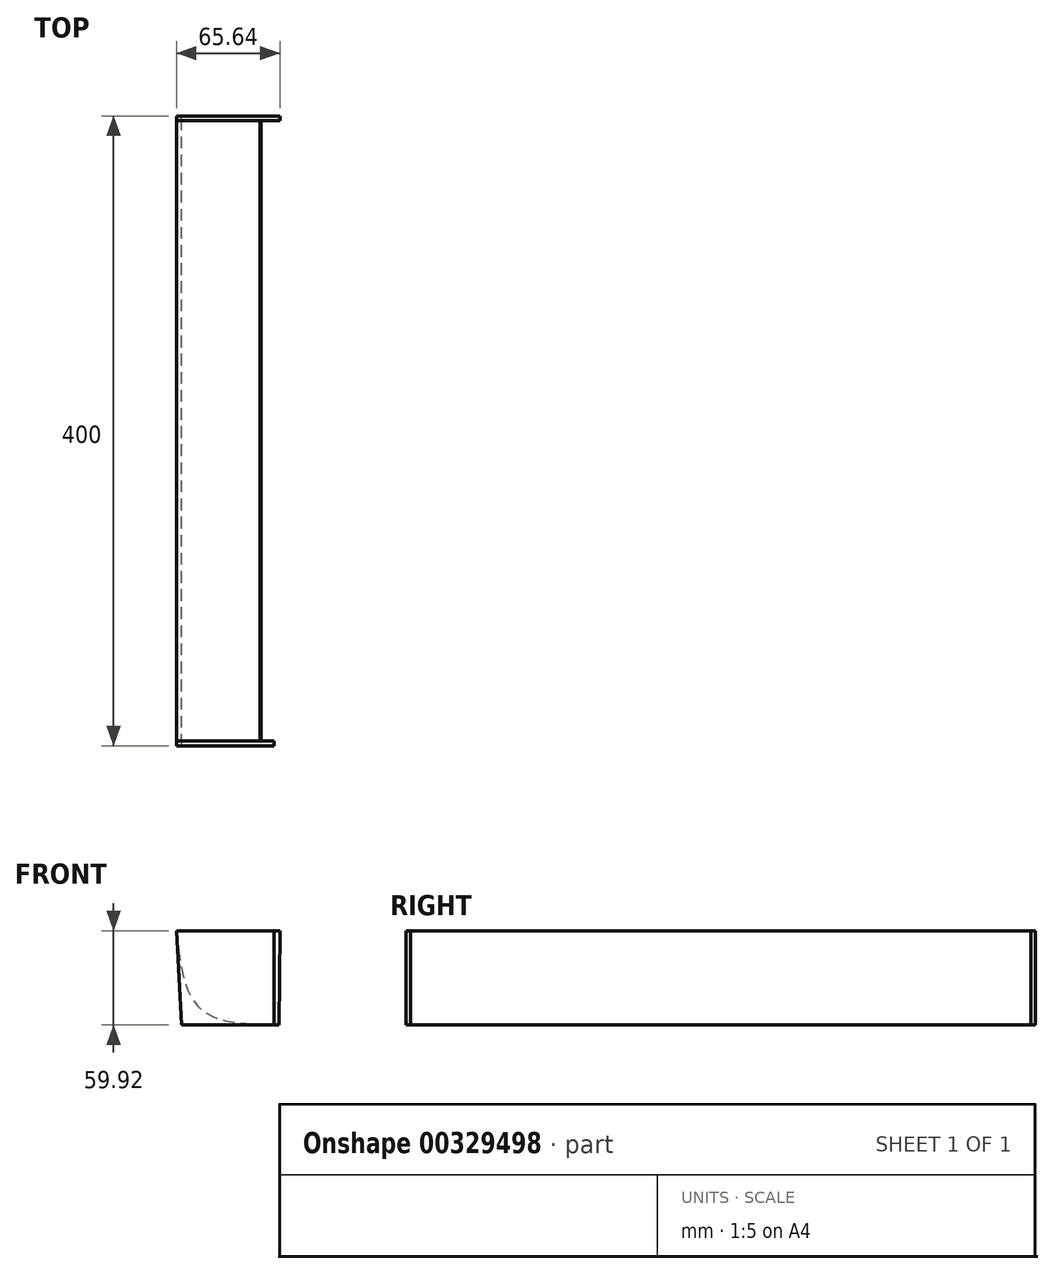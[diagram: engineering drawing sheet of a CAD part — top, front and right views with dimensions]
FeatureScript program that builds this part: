
annotation { "Feature Type Name" : "Feature", "Feature Type Description" : "" }
export const myFeature = defineFeature(function(context is Context, id is Id, definition is map)
    precondition{}
    {
        {
            var Q0;
            Q0=qCreatedBy(makeId("Front.planeOp"),FACE);
            var sketch = newSketch(context, id + "F0", { "sketchPlane" : qUnion([Q0])});
            skLineSegment(sketch, "E0", {"start": v(3.08, 0) * mm, "end": v(53.01, 0) * mm});
            skFitSpline(sketch, "E1", {"points": [v(0, 59.92) * mm, v(25.95, 4.2) * mm, v(53.01, 0) * mm], "startDerivative": vector(13.48, -155.54) * mm, "endDerivative": vector(-30.77, -7.46) * mm});
            skLineSegment(sketch, "E2", {"start": v(0, 59.92) * mm, "end": v(3.08, 0) * mm});
            skSolve(sketch);
        }
        {
            var Q0;
            Q0=makeQuery(id+"F0.imprint","IMPRINT",FACE,{"disambiguationData":[TD([[makeQuery(id+"F0.imprint","IMPRINT",EDGE,{"derivedFrom":sQuery(id+"F0.wireOp",EDGE,"E0")}),1.0]])]});
            extrude(context, id + "F1", {"entities" : qUnion([Q0]), "depth" : 400 * mm});
        }
        {
            var Q0;
            Q0=qCreatedBy(makeId("Front.planeOp"),FACE);
            var sketch = newSketch(context, id + "F2", { "sketchPlane" : qUnion([Q0])});
            skLineSegment(sketch, "E3", {"start": v(3.08, 0) * mm, "end": v(0, 59.92) * mm});
            skLineSegment(sketch, "E4", {"start": v(0, 59.92) * mm, "end": v(65.64, 59.92) * mm});
            skLineSegment(sketch, "E5", {"start": v(65.64, 59.92) * mm, "end": v(65.08, 0) * mm});
            skLineSegment(sketch, "E6", {"start": v(65.08, 0) * mm, "end": v(3.08, 0) * mm});
            skSolve(sketch);
        }
        {
            var Q0;
            Q0 = qSketchRegion(id + "F2", true);
            extrude(context, id + "F3", {"entities" : qUnion([Q0]), "operationType" : NewBodyOperationType.ADD, "depth" : 3 * mm});
        }
        {
            var Q0;
            Q0=qCreatedBy(makeId("Right.planeOp"),FACE);
            var sketch = newSketch(context, id + "F4", { "sketchPlane" : qUnion([Q0])});
            skLineSegment(sketch, "E7.bottom", {"start": v(-400, 59.92) * mm, "end": v(-397, 59.92) * mm});
            skLineSegment(sketch, "E7.top", {"start": v(-400, 0) * mm, "end": v(-397, 0) * mm});
            skLineSegment(sketch, "E7.left", {"start": v(-397, 59.92) * mm, "end": v(-397, 0) * mm});
            skLineSegment(sketch, "E7.right", {"start": v(-400, 59.92) * mm, "end": v(-400, 0) * mm});
            skSolve(sketch);
        }
        {
            var Q0;
            Q0 = qSketchRegion(id + "F4", true);
            extrude(context, id + "F5", {"entities" : qUnion([Q0]), "operationType" : NewBodyOperationType.ADD, "depth" : 62 * mm});
        }
        {
            var Q0;
            {var subQ0=sQuery(id+"F4.wireOp",EDGE,"E7.bottom");var subQ1=sQuery(id+"F4.wireOp",EDGE,"E7.left");var subQ2=sQuery(id+"F4.wireOp",EDGE,"E7.top");var subQ3=makeQuery(id+"F5.opExtrude","SWEPT_FACE",FACE,{"disambiguationData":[OSD([subQ1])]});Q0=makeQuery(id+"F5.boolean.opBoolean","SPLIT",FACE,{"disambiguationData":[TD([makeQuery(id+"F1.opExtrude","SWEPT_FACE",FACE,{"disambiguationData":[OSD([sQuery(id+"F0.wireOp",EDGE,"E0")])]}),makeQuery(id+"F1.opExtrude","SWEPT_FACE",FACE,{"disambiguationData":[OSD([sQuery(id+"F0.wireOp",EDGE,"E1")])]}),makeQuery(id+"F1.opExtrude","SWEPT_FACE",FACE,{"disambiguationData":[OSD([sQuery(id+"F0.wireOp",EDGE,"E2")])]}),makeQuery(id+"F3.opExtrude","SWEPT_FACE",FACE,{"disambiguationData":[OSD([sQuery(id+"F2.wireOp",EDGE,"E6")])]}),makeQuery(id+"F5.opExtrude","SWEPT_FACE",FACE,{"disambiguationData":[OSD([subQ0])]}),makeQuery(id+"F5.opExtrude","CAP_FACE",FACE,{"disambiguationData":[OSD([subQ0,subQ2,subQ1,sQuery(id+"F4.wireOp",EDGE,"E7.right")])],"isStart":true}),makeQuery(id+"F5.opExtrude","SWEPT_FACE",FACE,{"disambiguationData":[OSD([subQ2])]}),subQ3])],"derivedFrom":subQ3});}
            extrude(context, id + "F6", {"entities" : qUnion([Q0]), "operationType" : NewBodyOperationType.REMOVE, "oppositeDirection" : true, "depth" : 25 * mm});
        }
    });
